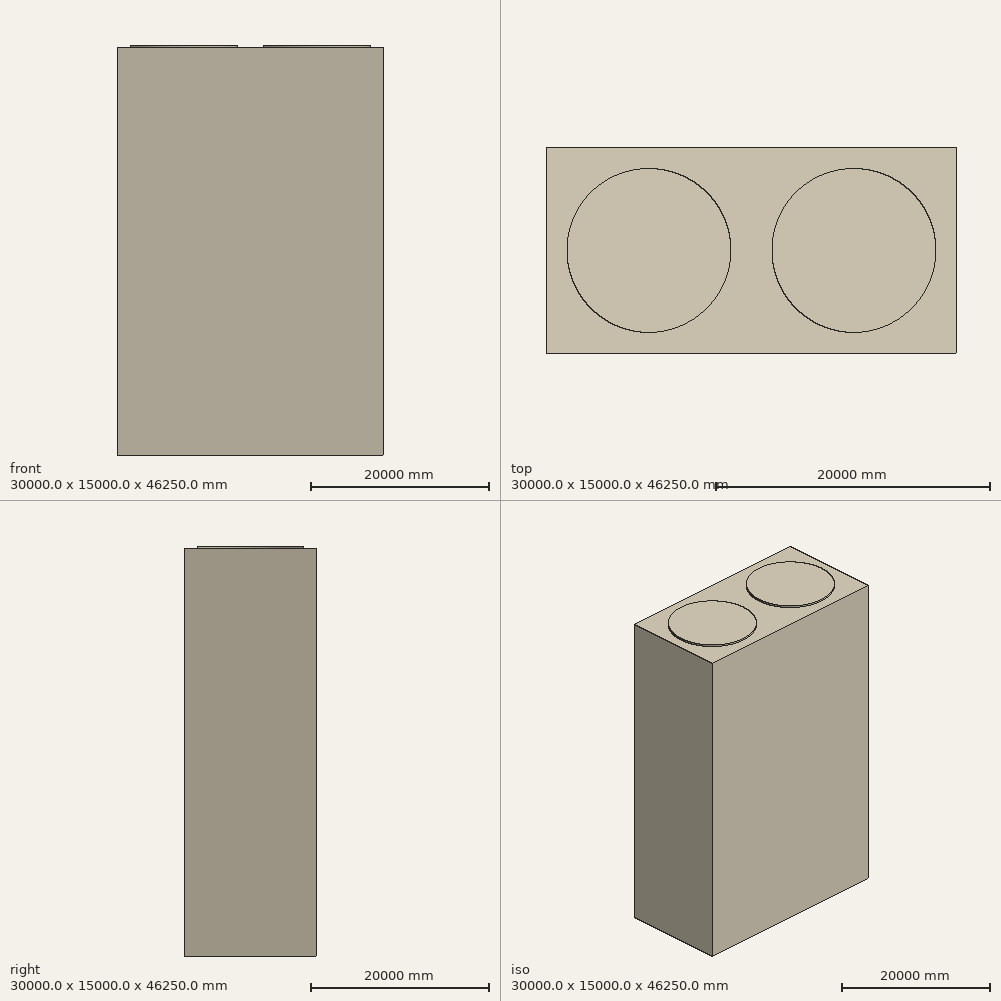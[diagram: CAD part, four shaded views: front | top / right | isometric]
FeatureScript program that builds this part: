
annotation { "Feature Type Name" : "Feature", "Feature Type Description" : "" }
export const myFeature = defineFeature(function(context is Context, id is Id, definition is map)
    precondition{}
    {
        {
            var Q0;
            Q0=qCreatedBy(makeId("Top.planeOp"),FACE);
            var sketch = newSketch(context, id + "F0", { "sketchPlane" : qUnion([Q0])});
            skLineSegment(sketch, "E0.bottom", {"start": v(15000, -7500) * mm, "end": v(-15000, -7500) * mm});
            skLineSegment(sketch, "E0.top", {"start": v(15000, 7500) * mm, "end": v(-15000, 7500) * mm});
            skLineSegment(sketch, "E0.left", {"start": v(15000, -7500) * mm, "end": v(15000, 7500) * mm});
            skLineSegment(sketch, "E0.right", {"start": v(-15000, -7500) * mm, "end": v(-15000, 7500) * mm});
            skPoint(sketch, "E0.middle", {"position": v(0, 0) * mm});
            skSolve(sketch);
        }
        {
            var Q0;
            Q0=makeQuery(id+"F0.imprint","IMPRINT",FACE,{"disambiguationData":[TD([[makeQuery(id+"F0.imprint","IMPRINT",EDGE,{"derivedFrom":sQuery(id+"F0.wireOp",EDGE,"E0.bottom")}),-1.0]])]});
            extrude(context, id + "F1", {"entities" : qUnion([Q0]), "depth" : 46000 * mm});
        }
        {
            var Q0;
            Q0=makeQuery(id+"F1.opExtrude","CAP_FACE",FACE,{"disambiguationData":[OSD([sQuery(id+"F0.wireOp",EDGE,"E0.bottom"),sQuery(id+"F0.wireOp",EDGE,"E0.top"),sQuery(id+"F0.wireOp",EDGE,"E0.left"),sQuery(id+"F0.wireOp",EDGE,"E0.right")])],"isStart":false});
            var sketch = newSketch(context, id + "F2", { "sketchPlane" : qUnion([Q0])});
            skSolve(sketch);
        }
        {
            var Q0;
            Q0=makeQuery(id+"F2.imprint","IMPRINT",FACE,{"disambiguationData":[TD([[makeQuery(id+"F2.imprint","IMPRINT",EDGE,{"derivedFrom":makeQuery(id+"F1.opExtrude","CAP_EDGE",EDGE,{"disambiguationData":[OSD([sQuery(id+"F0.wireOp",EDGE,"E0.bottom")])],"isStart":false})}),-1.0]])]});
            var sketch = newSketch(context, id + "F3", { "sketchPlane" : qUnion([Q0])});
            skLineSegment(sketch, "E1.0", {"start": v(-15000, -7500) * mm, "end": v(-15000, 7500) * mm, "construction": true});
            skLineSegment(sketch, "E2.0", {"start": v(15000, 7500) * mm, "end": v(-15000, 7500) * mm, "construction": true});
            skLineSegment(sketch, "E3.0", {"start": v(15000, -7500) * mm, "end": v(-15000, -7500) * mm, "construction": true});
            skLineSegment(sketch, "E4.0", {"start": v(15000, -7500) * mm, "end": v(15000, 7500) * mm, "construction": true});
            skLineSegment(sketch, "E5.0.0", {"start": v(-15000, -7500) * mm, "end": v(15000, -7500) * mm, "construction": true});
            skLineSegment(sketch, "E5.0.3", {"start": v(-15000, 7500) * mm, "end": v(-15000, -7500) * mm, "construction": true});
            skLineSegment(sketch, "E6", {"start": v(-15000, 0) * mm, "end": v(-7500, 0) * mm, "construction": true});
            skLineSegment(sketch, "E7", {"start": v(-7500, 0) * mm, "end": v(7500, 0) * mm, "construction": true});
            skLineSegment(sketch, "E8", {"start": v(7500, 0) * mm, "end": v(15000, 0) * mm, "construction": true});
            skCircle(sketch, "E9", {"center": v(-7500, 0) * mm, "radius": 6000 * mm});
            skCircle(sketch, "E10", {"center": v(7500, 0) * mm, "radius": 6000 * mm});
            skSolve(sketch);
        }
        {
            var Q0;
            Q0=makeQuery(id+"F3.imprint","IMPRINT",FACE,{"disambiguationData":[TD([[makeQuery(id+"F3.imprint","IMPRINT",EDGE,{"derivedFrom":sQuery(id+"F3.wireOp",EDGE,"E9")}),1.0]])]});
            var Q1;
            Q1=makeQuery(id+"F3.imprint","IMPRINT",FACE,{"disambiguationData":[TD([[makeQuery(id+"F3.imprint","IMPRINT",EDGE,{"derivedFrom":sQuery(id+"F3.wireOp",EDGE,"E10")}),1.0]])]});
            extrude(context, id + "F4", {"entities" : qUnion([Q0, Q1]), "operationType" : NewBodyOperationType.ADD, "depth" : 250 * mm});
        }
        {
            var Q0;
            Q0=makeQuery(id+"F4.opExtrude","CAP_FACE",FACE,{"disambiguationData":[OSD([sQuery(id+"F3.wireOp",EDGE,"E9")])],"isStart":false});
            var sketch = newSketch(context, id + "F5", { "sketchPlane" : qUnion([Q0])});
            skCircle(sketch, "E11", {"center": v(-13470, 0) * mm, "radius": 10 * mm});
            skCircle(sketch, "E12", {"center": v(-1530, 0) * mm, "radius": 10 * mm});
            skCircle(sketch, "E13.0", {"center": v(-7500, 0) * mm, "radius": 6000 * mm, "construction": true});
            skSolve(sketch);
        }
        {
            var Q0;
            Q0=makeQuery(id+"F5.imprint","IMPRINT",FACE,{"disambiguationData":[TD([[makeQuery(id+"F5.imprint","IMPRINT",EDGE,{"derivedFrom":sQuery(id+"F5.wireOp",EDGE,"E11")}),1.0]])]});
            var Q1;
            Q1=makeQuery(id+"F5.imprint","IMPRINT",FACE,{"disambiguationData":[TD([[makeQuery(id+"F5.imprint","IMPRINT",EDGE,{"derivedFrom":sQuery(id+"F5.wireOp",EDGE,"E12")}),1.0]])]});
            extrude(context, id + "F6", {"entities" : qUnion([Q0, Q1]), "operationType" : NewBodyOperationType.REMOVE, "oppositeDirection" : true, "depth" : 25 * mm});
        }
    });
